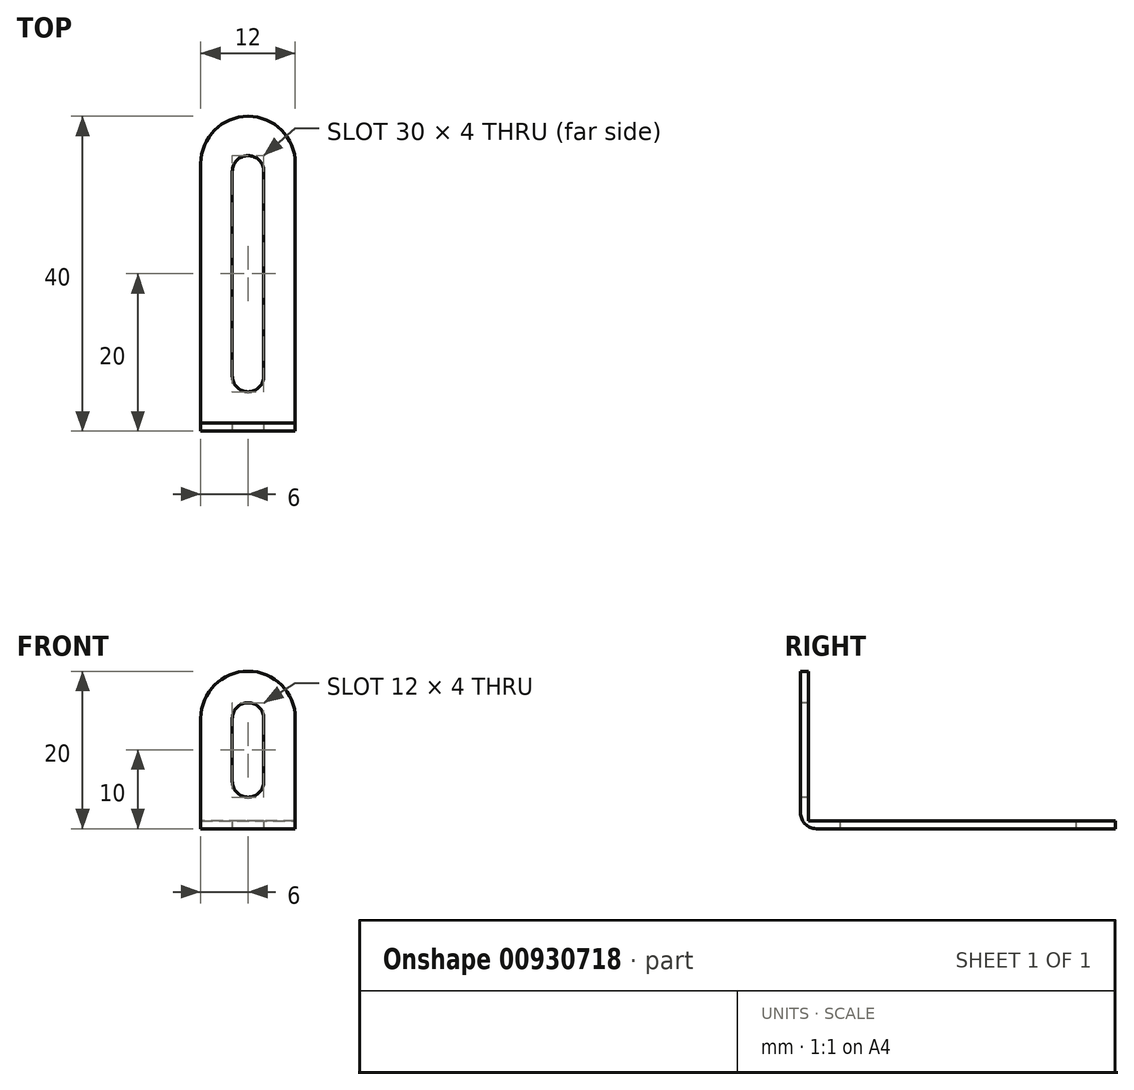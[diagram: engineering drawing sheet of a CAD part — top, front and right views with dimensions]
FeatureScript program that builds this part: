
annotation { "Feature Type Name" : "Feature", "Feature Type Description" : "" }
export const myFeature = defineFeature(function(context is Context, id is Id, definition is map)
    precondition{}
    {
        {
            var Q0;
            Q0=qCreatedBy(makeId("Front.planeOp"),FACE);
            var sketch = newSketch(context, id + "F0", { "sketchPlane" : qUnion([Q0])});
            skLineSegment(sketch, "E0.bottom", {"start": v(6, -10) * mm, "end": v(-6, -10) * mm});
            skLineSegment(sketch, "E0.top", {"start": v(0, 10) * mm, "end": v(0, 10) * mm});
            skLineSegment(sketch, "E0.left", {"start": v(6, -10) * mm, "end": v(6, 4) * mm});
            skLineSegment(sketch, "E0.right", {"start": v(-6, -10) * mm, "end": v(-6, 4) * mm});
            skPoint(sketch, "E0.middle", {"position": v(0, 0) * mm});
            skLineSegment(sketch, "E1.bottom", {"start": v(0, -6) * mm, "end": v(0, -6) * mm});
            skLineSegment(sketch, "E1.top", {"start": v(0, 6) * mm, "end": v(0, 6) * mm});
            skLineSegment(sketch, "E1.left", {"start": v(2, -4) * mm, "end": v(2, 4) * mm});
            skLineSegment(sketch, "E1.right", {"start": v(-2, -4) * mm, "end": v(-2, 4) * mm});
            skPoint(sketch, "E2.visualSharp", {"position": v(-2, -6) * mm});
            skArc(sketch, "E2.filletArc", {"start": v(-2, -4) * mm, "mid": v(-1.41, -5.41) * mm, "end": v(0, -6) * mm});
            skPoint(sketch, "E3.visualSharp", {"position": v(2, -6) * mm});
            skArc(sketch, "E3.filletArc", {"start": v(0, -6) * mm, "mid": v(1.41, -5.41) * mm, "end": v(2, -4) * mm});
            skPoint(sketch, "E4.visualSharp", {"position": v(2, 6) * mm});
            skArc(sketch, "E4.filletArc", {"start": v(2, 4) * mm, "mid": v(1.41, 5.41) * mm, "end": v(0, 6) * mm});
            skPoint(sketch, "E5.visualSharp", {"position": v(-2, 6) * mm});
            skArc(sketch, "E5.filletArc", {"start": v(0, 6) * mm, "mid": v(-1.41, 5.41) * mm, "end": v(-2, 4) * mm});
            skPoint(sketch, "E6.visualSharp", {"position": v(6, 10) * mm});
            skArc(sketch, "E6.filletArc", {"start": v(6, 4) * mm, "mid": v(4.24, 8.24) * mm, "end": v(0, 10) * mm});
            skPoint(sketch, "E7.visualSharp", {"position": v(-6, 10) * mm});
            skArc(sketch, "E7.filletArc", {"start": v(0, 10) * mm, "mid": v(-4.24, 8.24) * mm, "end": v(-6, 4) * mm});
            skSolve(sketch);
        }
        {
            var Q0;
            Q0=makeQuery(id+"F0.imprint","IMPRINT",FACE,{"disambiguationData":[TD([[makeQuery(id+"F0.imprint","IMPRINT",EDGE,{"derivedFrom":sQuery(id+"F0.wireOp",EDGE,"E1.left")}),-1.0]])]});
            extrude(context, id + "F1", {"entities" : qUnion([Q0]), "oppositeDirection" : true, "depth" : 1 * mm, "offsetDistance" : 25 * mm});
        }
        {
            var Q0;
            Q0=makeQuery(id+"F1.opExtrude","SWEPT_FACE",FACE,{"disambiguationData":[OSD([sQuery(id+"F0.wireOp",EDGE,"E0.bottom")])]});
            var sketch = newSketch(context, id + "F2", { "sketchPlane" : qUnion([Q0])});
            skLineSegment(sketch, "E8.bottom", {"start": v(0, -35) * mm, "end": v(0, -35) * mm});
            skLineSegment(sketch, "E8.top", {"start": v(0, -5) * mm, "end": v(0, -5) * mm});
            skLineSegment(sketch, "E8.left", {"start": v(2, -33) * mm, "end": v(2, -7) * mm});
            skLineSegment(sketch, "E8.right", {"start": v(-2, -33) * mm, "end": v(-2, -7) * mm});
            skPoint(sketch, "E9.visualSharp", {"position": v(-2, -5) * mm});
            skArc(sketch, "E9.filletArc", {"start": v(0, -5) * mm, "mid": v(-1.41, -5.59) * mm, "end": v(-2, -7) * mm});
            skPoint(sketch, "E10.visualSharp", {"position": v(2, -5) * mm});
            skArc(sketch, "E10.filletArc", {"start": v(2, -7) * mm, "mid": v(1.41, -5.59) * mm, "end": v(0, -5) * mm});
            skPoint(sketch, "E11.visualSharp", {"position": v(-2, -35) * mm});
            skArc(sketch, "E11.filletArc", {"start": v(-2, -33) * mm, "mid": v(-1.41, -34.41) * mm, "end": v(0, -35) * mm});
            skPoint(sketch, "E12.visualSharp", {"position": v(2, -35) * mm});
            skArc(sketch, "E12.filletArc", {"start": v(0, -35) * mm, "mid": v(1.41, -34.41) * mm, "end": v(2, -33) * mm});
            skLineSegment(sketch, "E13.bottom", {"start": v(-6, 0) * mm, "end": v(6, 0) * mm});
            skLineSegment(sketch, "E13.top", {"start": v(0, -40) * mm, "end": v(0, -40) * mm});
            skLineSegment(sketch, "E13.left", {"start": v(-6, 0) * mm, "end": v(-6, -34) * mm});
            skLineSegment(sketch, "E13.right", {"start": v(6, 0) * mm, "end": v(6, -34) * mm});
            skPoint(sketch, "E14.visualSharp", {"position": v(6, -40) * mm});
            skArc(sketch, "E14.filletArc", {"start": v(0, -40) * mm, "mid": v(4.24, -38.24) * mm, "end": v(6, -34) * mm});
            skPoint(sketch, "E15.visualSharp", {"position": v(-6, -40) * mm});
            skArc(sketch, "E15.filletArc", {"start": v(-6, -34) * mm, "mid": v(-4.24, -38.24) * mm, "end": v(0, -40) * mm});
            skSolve(sketch);
        }
        {
            var Q0;
            Q0=makeQuery(id+"F2.imprint","IMPRINT",FACE,{"disambiguationData":[TD([[makeQuery(id+"F2.imprint","IMPRINT",EDGE,{"derivedFrom":sQuery(id+"F2.wireOp",EDGE,"E8.left")}),-1.0]])]});
            extrude(context, id + "F3", {"entities" : qUnion([Q0]), "operationType" : NewBodyOperationType.ADD, "oppositeDirection" : true, "depth" : 1 * mm, "offsetDistance" : 25 * mm});
        }
        {
            var Q0;
            Q0=makeQuery(id+"F1.opExtrude","CAP_EDGE",EDGE,{"disambiguationData":[OSD([sQuery(id+"F0.wireOp",EDGE,"E0.bottom")])],"isStart":true});
            fillet(context, id + "F4", {"entities" : qUnion([Q0]), "radius" : 2 * mm, "tangentPropagation" : true, "allowEdgeOverflow" : false});
        }
    });
